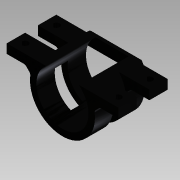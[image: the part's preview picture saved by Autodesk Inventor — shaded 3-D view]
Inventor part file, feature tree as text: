
AUTODESK INVENTOR PART (.ipt)
format: ipt  version: 2015 SP1 (Build 190203100, 203)  size: 271,360 bytes
history: native  units: mm
features: extrude x8, sketch x8, mirror x1, fillet x1, projected_geometry x1
ambient origin geometry x8: Origin, YZ Plane, XZ Plane, XY Plane, X Axis, Y Axis, Z Axis, Center Point
bodies: Solid1 (feature_tree)
feature tree (19):
  extrude  "Extrusion1"  TaperAngle=45.0deg  [1 undecoded]
  extrude  "Extrusion2"  Depth=2.0mm
  extrude  "Extrusion3"  Depth=10.0mm
  mirror  "Mirror2"
  extrude  "Extrusion7"  Depth=5.0mm
  extrude  "Extrusion8"  Depth=10.0mm
  fillet  "Fillet1"  Radius=10.0mm
  extrude  "Extrusion9"  Depth=5.0mm
  extrude  "Extrusion10"  Depth=5.0mm
  extrude  "Extrusion11"  Depth=2.0mm
  sketch  "Sketch1"  dims[d9=135.0deg d10=45.0deg]
  sketch  "Sketch2"  dims[d21=2.0mm d22=25.4mm]
  sketch  "Sketch3"  dims[d23=10.0mm d24=0.0mm d25=3.5mm]
  sketch  "Sketch13"  dims[d26=3.5mm d27=5.0mm]
  sketch  "Sketch14"  dims[d28=5.0mm d30=12.700083mm d31=10.0mm d32=0.0mm]
  sketch  "Sketch15"  dims[d39=3.5mm d40=0.0mm d55=5.0mm]
  sketch  "Sketch18"  dims[d60=5.0mm d61=5.0mm]
  sketch  "Sketch19"  dims[d62=3.5mm d63=3.5mm d64=5.0mm d65=3.0mm d66=0.0mm d67=3.0mm d68=0.0mm d69=2.0mm d71=1.5mm d72=27.0mm d73=0.0mm d74=27.0mm d75=0.0mm d76=200.0mm d77=0.0mm]
  projected_geometry  "Projected Loop8"
note: 1 required parameter value undecoded (feature->parameter linkage not recoverable at this tier; creation-order binding heuristic only, values carry confidence <= 0.55)
